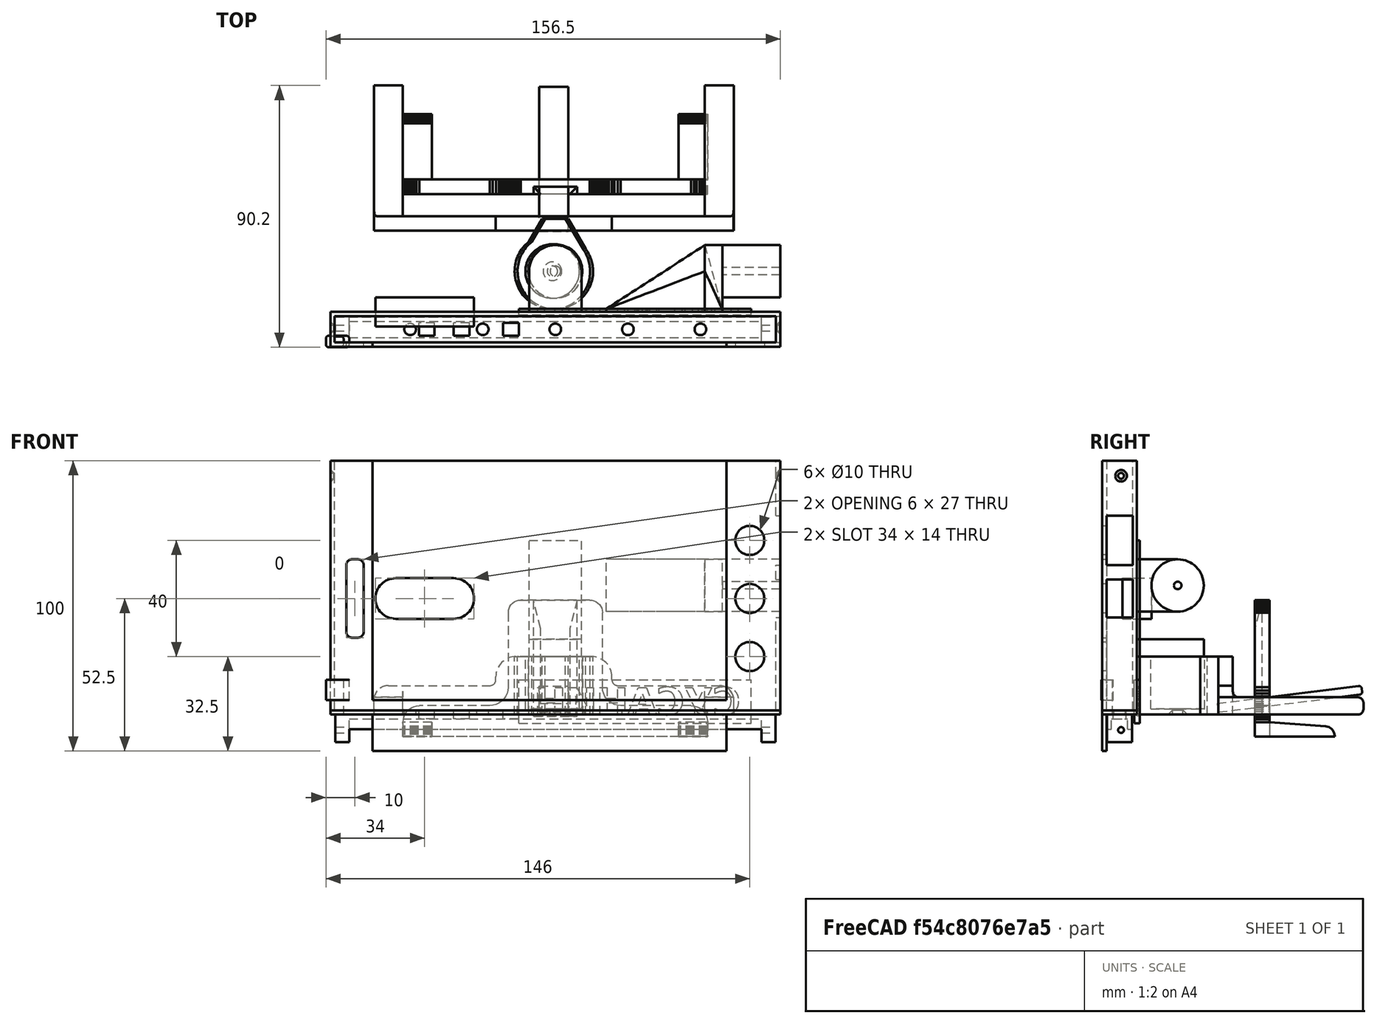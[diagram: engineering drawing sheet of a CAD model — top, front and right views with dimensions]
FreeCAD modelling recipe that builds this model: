
FCSTD DOCUMENT  (FreeCAD 0.18.4R)
Label: phone_nav_convertor
License: All rights reserved
LicenseURL: http://en.wikipedia.org/wiki/All_rights_reserved
objects: Part::Box×22, Part::Cylinder×9, Part::Fillet×8, Part::MultiFuse×7, Part::Feature×6, App::Part×6, Part::Cut×5, Part::FeaturePython×4, Part::Extrusion×4, Sketcher::SketchObject×3, Part::Compound×3, Mesh::Feature×2, Part::Part2DObjectPython×2, Part::RuledSurface×2, PartDesign::Body×2, Spreadsheet::Sheet×1, Part::Loft×1, PartDesign::Pad×1, PartDesign::FeatureBase×1, Part::Mirroring×1
note: 82 computed .brp shape members not serialized (recipe doc carries the construction recipe); baked Part::Feature solids carry a one-line shape summary decoded from their .brp

FEATURE [Part::Box] Box  label="pocket cube"
  AttacherType = Attacher::AttachEngine3D
  Height = 177
  Length = 152
  Placement = pos=(1.5,1.5,1.5) rot=(0,0,1;0rad)
  Width = 9
  expr: Placement.Base.x = p.wall
  expr: Placement.Base.y = p.wall
  expr: Placement.Base.z = p.wall
  expr: Height = p.phone_pocket_height + 100
  expr: Width = p.phone_pocket_width
  expr: Length = p.phone_pocket_length
FEATURE [Part::Box] Box001  label="wall cube"
  AttacherType = Attacher::AttachEngine3D
  Height = 87.5
  Length = 155
  Width = 12
  expr: Height = p.phone_pocket_height + 2 * p.wall + p.top_extra_height
  expr: Width = p.phone_pocket_width + 2 * p.wall
  expr: Length = p.phone_pocket_length + 2 * p.wall
FEATURE [Spreadsheet::Sheet] Spreadsheet  label="p"
  cells = A1=phone_pocket_width; B1(phone_pocket_width)=9; A2=phone_pocket_length; B2(phone_pocket_length)=152; A3=phone_pocket_height; B3(phone_pocket_height)=77; A4=wall; B4(wall)=1.5; A5=display_length; B5(display_length)=122; A6=display_height; B6(display_height)=70; A7=display_z_offset; B7(display_z_offset)==(p.phone_pocket_height - p.display_height) / 2; A8=display_btn_side_offset; B8(display_btn_side_offset)=16; A9=display_cam_side_offset; B9(display_cam_side_offset)=13; A10=cam_side_hole_length; B10(cam_side_hole_length)=6; A11=cam_side_hole_height; B11(cam_side_hole_height)=27; A12=cam_size_hole_z_offset; B12(cam_size_hole_z_offset)==(p.phone_pocket_height - p.cam_side_hole_height) / 2; A13=cam_side_hole_x_offset; B13(cam_side_hole_x_offset)=4; A14=speaker_height; B14(speaker_height)=17; A15=speaker_z_offset; B15(speaker_z_offset)=50; A16=usb_hole_height; B16(usb_hole_height)=13; A17=usb_hole_z_offset; B17(usb_hole_z_offset)=32; A18=top_extra_height; B18(top_extra_height)=7.5; A19=button_radius; B19(button_radius)=5; A20=button_z_dist; B20(button_z_dist)=20; A21=button_z_offset; B21(button_z_offset)==(p.phone_pocket_height - 2 * p.button_z_dist) / 2; A22=button_x_offset; B22(button_x_offset)=9; A23=cylinder_radius; B23(cylinder_radius)=9; A24=cylinder_height; B24(cylinder_height)=20; A25=cylinder_dist; B25(cylinder_dist)==p.phone_pocket_width + 2 * p.wall + p.cylinder_radius + 5; A26=enforcement_length; B26(enforcement_length)==p.cylinder_radius * 2; A27=enforcement_height; B27(enforcement_height)=40; A28=enforcement_width; B28(enforcement_width)=1; A29=bottom_hole_count; B29(bottom_hole_count)=5; A30=bottom_hole_dist; B30(bottom_hole_dist)=25; A31=bottom_hole_radius; B31(bottom_hole_radius)=2; A32=phone_btn1_offset; B32(phone_btn1_offset)=29; A33=phone_btn2_offset; B33(phone_btn2_offset)=41; A34=phone_btn3_offset; B34(phone_btn3_offset)=58; A35=phone_btn_length; B35(phone_btn_length)=5; A36=phone_btn_width; B36(phone_btn_width)=4; A37=camera_x_dist; B37(camera_x_dist)==p.phone_pocket_length - 21; A38=camera_y_dist; B38(camera_y_dist)==p.phone_pocket_height / 2; A39=camera_radius; B39(camera_radius)=7; A40=camera_finger_dist; B40(camera_finger_dist)=20; A41=finger_radius; B41(finger_radius)=7
FEATURE [Part::Box] Box002  label="display hole cube"
  AttacherType = Attacher::AttachEngine3D
  Height = 170
  Length = 122
  Placement = pos=(14.5,-10.5,5) rot=(0,0,1;0rad)
  Width = 20
  expr: Placement.Base.y = -p.phone_pocket_width - p.wall
  expr: Placement.Base.x = p.display_cam_side_offset + p.wall
  expr: Placement.Base.z = p.display_z_offset + p.wall
  expr: Height = p.display_height + 100
  expr: Length = p.display_length
FEATURE [Part::Box] Box003  label="speaker hole cube"
  AttacherType = Attacher::AttachEngine3D
  Height = 17
  Length = 10
  Placement = pos=(151,1.5,51.5) rot=(0,0,1;0rad)
  Width = 9
  expr: Placement.Base.y = p.wall
  expr: Width = p.phone_pocket_width
  expr: Placement.Base.z = p.speaker_z_offset + p.wall
  expr: Height = p.speaker_height
FEATURE [Part::Box] Box004  label="usb hole cube"
  AttacherType = Attacher::AttachEngine3D
  Height = 13
  Length = 10
  Placement = pos=(151,1.5,33.5) rot=(0,0,1;0rad)
  Width = 9
  expr: Placement.Base.y = p.wall
  expr: Placement.Base.z = p.usb_hole_z_offset + p.wall
  expr: Height = p.usb_hole_height
  expr: Width = p.phone_pocket_width
FEATURE [Part::Box] Box005  label="cam side hole cube"
  AttacherType = Attacher::AttachEngine3D
  Height = 27
  Length = 6
  Placement = pos=(5.5,-4,26.5) rot=(0,0,1;0rad)
  Width = 10
  expr: Placement.Base.x = p.wall + p.cam_side_hole_x_offset
  expr: Placement.Base.z = p.cam_size_hole_z_offset + p.wall
  expr: Height = p.cam_side_hole_height
  expr: Length = p.cam_side_hole_length
FEATURE [Part::Cylinder] Cylinder
  Angle = 360
  AttacherType = Attacher::AttachEngine3D
  Height = 10
  Placement = pos=(144.5,5,20) rot=(1,0,0;1.5708rad)
  Radius = 5
  expr: Placement.Base.x = p.wall + p.phone_pocket_length - p.button_x_offset
  expr: Placement.Base.z = p.button_z_offset + p.wall
FEATURE [Part::FeaturePython] Array  # Draft array (typed FeaturePython)
  Angle = 360
  ArrayType = 0
  Axis = (0,0,1)
  Base = -> Cylinder
  Center = (0,0,0)
  Fuse = false
  IntervalAxis = (0,0,0)
  IntervalX = (1,0,0)
  IntervalY = (0,1,0)
  IntervalZ = (0,0,20)
  NumberPolar = 1
  NumberX = 1
  NumberY = 1
  NumberZ = 3
  expr: IntervalZ.z = p.button_z_dist
FEATURE [Mesh::Feature] Plate
  Placement = pos=(68,34,26) rot=(-0.57735,-0.57735,0.57735;4.18879rad)
FEATURE [Part::Feature] Plate001
  Placement = pos=(0,31.2,0.6) rot=(0,0,1;0rad)
  shape: bbox 13 x 2.3 x 40 mm, 12 faces, 0 solids (baked)
FEATURE [Part::Cylinder] Cylinder001  label="side screw holes"
  Angle = 360
  AttacherType = Attacher::AttachEngine3D
  Height = 200
  Placement = pos=(-27,6.5,82.25) rot=(0,1,0;1.5708rad)
  Radius = 1
  expr: Placement.Base.z = p.wall + p.phone_pocket_height + p.top_extra_height / 2
FEATURE [Part::Cylinder] Cylinder002
  Angle = 360
  AttacherType = Attacher::AttachEngine3D
  Height = 20
  Placement = pos=(77.5,26,0) rot=(0,0,1;0rad)
  Radius = 9
  expr: Height = p.cylinder_height
  expr: Radius = p.cylinder_radius
  expr: Placement.Base.y = p.cylinder_dist
  expr: Placement.Base.x = p.phone_pocket_length / 2 + p.wall
FEATURE [Sketcher::SketchObject] Sketch
  MapMode = 5
  expr: Constraints[10] = p.cylinder_dist - 2 * p.wall - p.phone_pocket_width
  expr: Constraints[7] = p.cylinder_radius
  expr: Constraints[3] = p.cylinder_radius * 2
  expr: Constraints[9] = p.phone_pocket_length / 2 + p.wall - p.cylinder_radius
  expr: Constraints[8] = p.phone_pocket_width + 2 * p.wall
  sketch-geometry (4):
    g0: LineSegment StartX=68.5 StartY=12 StartZ=0 EndX=86.5 EndY=12 EndZ=0
    g1: LineSegment StartX=86.5 StartY=12 StartZ=0 EndX=86.5 EndY=26 EndZ=0
    g2: LineSegment StartX=68.5 StartY=12 StartZ=0 EndX=68.5 EndY=26 EndZ=0
    g3: ArcOfCircle CenterX=77.5 CenterY=26 CenterZ=0 NormalX=0 NormalY=0 NormalZ=1 AngleXU=0 Radius=9 StartAngle=0 EndAngle=3.14159
  constraints (11):
    c: Horizontal(g0)
    c: Coincident(g1,g0)
    c: Coincident(g2,g0)
    c: DistanceX(g0,g0) = 18
    c: DistanceY(g2,g1) = 0
    c: Tangent(g2,g3) = 1.5708
    c: Tangent(g3,g1) = -1.5708
    c: Radius(g3) = 9
    c: DistanceY(g-1,g0) = 12
    c: DistanceX(g-1,g0) = 68.5
    c: DistanceY(g2,g2) = 14
FEATURE [Part::Extrusion] Extrude
  Base = -> Sketch
  Dir = (0,0,1)
  DirMode = 2
  FaceMakerClass = Part::FaceMakerBullseye
  LengthFwd = 6
  LengthRev = 0
  Placement = pos=(0,0,20) rot=(0,0,1;0rad)
  Solid = true
  Symmetric = false
  expr: Placement.Base.z = p.cylinder_height
FEATURE [Part::Box] Box006  label="enforcement cube"
  AttacherType = Attacher::AttachEngine3D
  Height = 40
  Length = 18
  Placement = pos=(68.5,12,20) rot=(0,0,1;0rad)
  Width = 1
  expr: Placement.Base.y = p.phone_pocket_width + p.wall * 2
  expr: Placement.Base.x = p.phone_pocket_length / 2 + p.wall - p.enforcement_length / 2
  expr: Width = p.enforcement_width
  expr: Length = p.enforcement_length
  expr: Placement.Base.z = p.cylinder_height
  expr: Height = p.enforcement_height
FEATURE [Part::Cylinder] Cylinder003
  Angle = 360
  AttacherType = Attacher::AttachEngine3D
  Height = 100
  Placement = pos=(77.5,26,-50) rot=(0,0,1;0rad)
  Radius = 1.3
  expr: Placement.Base.y = p.cylinder_dist
  expr: Placement.Base.x = p.phone_pocket_length / 2 + p.wall
FEATURE [Part::Cut] Cut001  label="Cylinder Cut"
  Base = -> Cylinder002
  Tool = -> Cylinder003
FEATURE [Part::Cylinder] Cylinder004  label="bottom_hole"
  Angle = 360
  AttacherType = Attacher::AttachEngine3D
  Height = 20
  Placement = pos=(27.5,6,-10) rot=(0,0,1;0rad)
  Radius = 2
  expr: Radius = p.bottom_hole_radius
  expr: Placement.Base.x = (p.phone_pocket_length + 2 * p.wall - (p.bottom_hole_count - 1) * p.bottom_hole_dist) / 2
  expr: Placement.Base.y = p.wall + p.phone_pocket_width / 2
FEATURE [Part::FeaturePython] Array001  label="bottom hole array"  # Draft array (typed FeaturePython)
  Angle = 360
  ArrayType = 0
  Axis = (0,0,1)
  Base = -> Cylinder004
  Center = (0,0,0)
  Fuse = false
  IntervalAxis = (0,0,0)
  IntervalX = (25,0,0)
  IntervalY = (0,1,0)
  IntervalZ = (0,0,1)
  NumberPolar = 1
  NumberX = 5
  NumberY = 1
  NumberZ = 1
  expr: NumberX = p.bottom_hole_count
  expr: IntervalX.x = p.bottom_hole_dist
FEATURE [Part::Part2DObjectPython] ShapeString  # Draft 2D object (typed FeaturePython)
  FontFile = <path>
  Placement = pos=(141.21,12,0) rot=(0,0.707107,0.707107;3.14159rad)
  Size = 10
  String = СУСАНИН
  Tracking = 0
FEATURE [Part::Extrusion] Extrude001  label="Susanin_label"
  Base = -> ShapeString
  Dir = (1e-16,1,0)
  DirMode = 2
  FaceMakerClass = Part::FaceMakerBullseye
  LengthFwd = 10
  LengthRev = 0
  Solid = false
  Symmetric = false
FEATURE [Part::Box] Box007  label="Cube"
  AttacherType = Attacher::AttachEngine3D
  Height = 15
  Length = 80
  Placement = pos=(65,11,-3) rot=(0,0,1;0rad)
  Width = 2
FEATURE [Part::Cut] Cut002
  Base = -> Box007
  Tool = -> Extrude001
FEATURE [App::Part] Part001  label="label plate part"
  Group = -> [ShapeString,Extrude001,Box007,Cut002]
  Origin = -> Origin001
  Placement = pos=(-27,5,68) rot=(0,0,1;0rad)
FEATURE [Part::Part2DObjectPython] ShapeString001  # Draft 2D object (typed FeaturePython)
  FontFile = <path>
  Placement = pos=(141.21,12,0) rot=(0,0.707107,0.707107;3.14159rad)
  Size = 10
  String = СУСАНИН
  Tracking = 0
FEATURE [Part::Extrusion] Extrude002  label="Susanin_label001"
  Base = -> ShapeString001
  Dir = (0,1,-2e-16)
  DirMode = 2
  FaceMakerClass = Part::FaceMakerBullseye
  LengthFwd = 1
  LengthRev = 0
  Solid = false
  Symmetric = false
FEATURE [App::Part] Part002  label="label part"
  Group = -> [ShapeString001,Extrude002]
  Origin = -> Origin002
  Placement = pos=(-27,5,68) rot=(0,0,1;0rad)
FEATURE [Part::RuledSurface] Ruled_Surface
  Curve1 = -> Extrude [Edge10]
  Curve2 = -> Box006 [Edge12]
  Orientation = 0
FEATURE [Part::RuledSurface] Ruled_Surface001
  Curve1 = -> Box006 [Edge3]
  Curve2 = -> Box006 [Edge7]
  Orientation = 0
  Placement = pos=(68.5,12,20) rot=(0,0,1;0rad)
FEATURE [Part::Loft] Loft
  Closed = false
  MaxDegree = 5
  Ruled = true
  Sections = -> [Ruled_Surface,Ruled_Surface001]
  Solid = true
FEATURE [Part::MultiFuse] Fusion001
  Shapes = -> [Loft,Cut001]
FEATURE [Part::Feature] Box006_rev  label="enforcement cube (Rev)"
  Placement = pos=(68.5,12,20) rot=(0,0,1;0rad)
  shape: bbox 18 x 1 x 40 mm, 6 faces (baked)
FEATURE [Part::Feature] Extrude003  label="Extrude001"
  shape: bbox 18 x 23 x 6 mm, 6 faces (baked)
FEATURE [Part::Cylinder] Cylinder005  label="Cylinder004"
  Angle = 360
  AttacherType = Attacher::AttachEngine3D
  Height = 30
  Placement = pos=(77.5,26,2) rot=(0,0,1;0rad)
  Radius = 9.3
  expr: Radius = p.cylinder_radius + 0.3
FEATURE [Part::Cylinder] Cylinder006  label="Cylinder005"
  Angle = 360
  AttacherType = Attacher::AttachEngine3D
  Height = 20
  Placement = pos=(77.5,26,0) rot=(0,0,1;0rad)
  Radius = 13
  expr: Height = p.cylinder_height
  expr: Radius = p.cylinder_radius + 4
FEATURE [PartDesign::Body] Body
  Origin = -> Origin004
  Placement = pos=(-0.4,0.5,0) rot=(0,0,1;0rad)
FEATURE [Sketcher::SketchObject] Sketch001
  MapMode = 5
  sketch-geometry (4):
    g0: LineSegment StartX=74 StartY=44 StartZ=0 EndX=68 EndY=33.7847 EndZ=0
    g1: LineSegment StartX=68 StartY=33.7847 StartZ=0 EndX=88 EndY=33.7847 EndZ=0
    g2: LineSegment StartX=88 StartY=33.7847 StartZ=0 EndX=82 EndY=44 EndZ=0
    g3: LineSegment StartX=82 StartY=44 StartZ=0 EndX=74 EndY=44 EndZ=0
  constraints (10):
    c: Coincident(g0,g1)
    c: Horizontal(g1)
    c: Coincident(g1,g2)
    c: Coincident(g2,g3)
    c: Coincident(g3,g0)
    c: Horizontal(g3)
    c: DistanceX(g3,g3) = 8
    c: DistanceX(g-1,g0) = 74
    c: DistanceX(g2,g1) = 6
    c: DistanceX(g0,g0) = 6
FEATURE [PartDesign::Pad] Pad
  Length = 20
  Length2 = 100
  Profile = -> Sketch001
  Type = 0
FEATURE [Part::MultiFuse] Fusion002
  Shapes = -> [Cylinder006,Pad]
FEATURE [Part::Cylinder] Cylinder007  label="Cylinder006"
  Angle = 360
  AttacherType = Attacher::AttachEngine3D
  Height = 30
  Placement = pos=(77.5,26,0) rot=(0,0,1;0rad)
  Radius = 1.8
FEATURE [Part::MultiFuse] Fusion003
  Shapes = -> [Cylinder005,Cylinder007]
FEATURE [Part::Cut] Cut003
  Base = -> Fusion002
  Tool = -> Fusion003
FEATURE [Part::FeaturePython] Countersunk001  # WARN: FeaturePython — macro-defined, semantics opaque (R4)
  Placement = pos=(-1,0,0) rot=(0,0,1;0rad)
  baseObject = -> Cut003
  diameters = Edge10:M3:0:0:Default
FEATURE [Part::Box] Box008  label="Cube001"
  AttacherType = Attacher::AttachEngine3D
  Height = 1.5
  Length = 155
  Width = 12
  expr: Height = p.wall
  expr: Width = p.phone_pocket_width + 2 * p.wall
  expr: Length = p.phone_pocket_length + 2 * p.wall
FEATURE [Part::Box] Box009  label="Cube002"
  AttacherType = Attacher::AttachEngine3D
  Height = 9.5
  Length = 151.6
  Placement = pos=(1.7,1.7,-9.5) rot=(0,0,1;0rad)
  Width = 8.6
  expr: Width = p.phone_pocket_width - 0.4
  expr: Length = p.phone_pocket_length - 0.4
  expr: Height = p.wall + p.top_extra_height + 0.5
  expr: Placement.Base.z = -p.top_extra_height - p.wall - 0.5
  expr: Placement.Base.y = p.wall + 0.2
  expr: Placement.Base.x = p.wall + 0.2
FEATURE [Part::Box] Box010  label="Cube003"
  AttacherType = Attacher::AttachEngine3D
  Height = 9.5
  Length = 142
  Placement = pos=(6.5,3.2,-11) rot=(0,0,1;0rad)
  Width = 5.6
  expr: Width = p.phone_pocket_width - 2 * p.wall - 0.4
  expr: Length = p.phone_pocket_length - 10
  expr: Height = p.top_extra_height + 2
  expr: Placement.Base.z = -p.wall - p.top_extra_height - 2
  expr: Placement.Base.y = p.wall * 2 + 0.2
  expr: Placement.Base.x = p.wall + 5
FEATURE [Part::Cylinder] Cylinder008  label="side screw holes001"
  Angle = 360
  AttacherType = Attacher::AttachEngine3D
  Height = 200
  Placement = pos=(-27,6.5,-5.3) rot=(0,1,0;1.5708rad)
  Radius = 1
FEATURE [Mesh::Feature] Support2_0  label="Support2.0"
FEATURE [Part::Feature] Support2_0001  label="Support2 shape"
  Placement = pos=(130,69,-24) rot=(0,0,1;3.14159rad)
  shape: bbox 105 x 27.5 x 47.09 mm, 356 faces, 0 solids (baked)
FEATURE [Part::Feature] Support2_0001_solid  label="Support2 shape (Solid)"
  shape: bbox 105 x 27.5 x 47.09 mm, 356 faces (baked)
FEATURE [Part::Box] Box013  label="btn cube"
  AttacherType = Attacher::AttachEngine3D
  Height = 12
  Length = 4.6
  Width = 3.6
  expr: Height = p.top_extra_height + 3 + p.wall
  expr: Width = p.phone_btn_width - 0.4
  expr: Length = p.phone_btn_length - 0.4
FEATURE [Part::Box] Box014  label="btn hole cube1"
  AttacherType = Attacher::AttachEngine3D
  Height = 20
  Length = 5.4
  Placement = pos=(30.5,3.8,-7.5) rot=(0,0,1;0rad)
  Width = 4.4
  expr: Placement.Base.x = p.wall + p.phone_btn1_offset
  expr: Placement.Base.y = p.wall + p.phone_pocket_width / 2 - p.phone_btn_width / 2 - 0.2
  expr: Placement.Base.z = -p.top_extra_height
  expr: Width = p.phone_btn_width + 0.4
  expr: Length = p.phone_btn_length + 0.4
FEATURE [Part::Box] Box015  label="btn hole cube2"
  AttacherType = Attacher::AttachEngine3D
  Height = 20
  Length = 5.4
  Placement = pos=(42.5,3.8,-7.5) rot=(0,0,1;0rad)
  Width = 4.4
  expr: Placement.Base.x = p.wall + p.phone_btn2_offset
  expr: Placement.Base.y = p.wall + p.phone_pocket_width / 2 - p.phone_btn_width / 2 - 0.2
  expr: Placement.Base.z = -p.top_extra_height
  expr: Width = p.phone_btn_width + 0.4
  expr: Length = p.phone_btn_length + 0.4
FEATURE [Part::Box] Box016  label="btn hole cube3"
  AttacherType = Attacher::AttachEngine3D
  Height = 20
  Length = 5.4
  Placement = pos=(59.5,3.8,-7.5) rot=(0,0,1;0rad)
  Width = 4.4
  expr: Placement.Base.x = p.wall + p.phone_btn3_offset
  expr: Placement.Base.y = p.wall + p.phone_pocket_width / 2 - p.phone_btn_width / 2 - 0.2
  expr: Placement.Base.z = -p.top_extra_height
  expr: Width = p.phone_btn_width + 0.4
  expr: Length = p.phone_btn_length + 0.4
FEATURE [Part::Box] Box017  label="btn rim cube"
  AttacherType = Attacher::AttachEngine3D
  Height = 7
  Length = 8
  Placement = pos=(-1.5,-0.2,5) rot=(0,0,1;0rad)
  Width = 4
  expr: Placement.Base.x = -p.wall
  expr: Height = p.top_extra_height + 3 + p.wall - 5
  expr: Width = p.phone_btn_width
  expr: Length = p.phone_btn_length + 2 * p.wall
FEATURE [Part::Box] Box018  label="Cube006"
  AttacherType = Attacher::AttachEngine3D
  Height = 12.5
  Length = 121.8
  Placement = pos=(14.6,0,-12.5) rot=(0,0,1;0rad)
  Width = 1.5
  expr: Width = p.wall
  expr: Length = p.display_length - 0.2
  expr: Height = (p.phone_pocket_height - p.display_height) / 2 + p.top_extra_height + p.wall
  expr: Placement.Base.z = -(p.phone_pocket_height - p.display_height) / 2 - p.top_extra_height - p.wall
  expr: Placement.Base.x = p.display_cam_side_offset + p.wall + 0.1
FEATURE [Part::MultiFuse] Fusion004
  Shapes = -> [Box008,Box009,Box018]
FEATURE [Part::Box] Box019  label="Cube007"
  AttacherType = Attacher::AttachEngine3D
  Height = 6
  Length = 142
  Placement = pos=(6.5,1.5,-11) rot=(0,0,1;0rad)
  Width = 9
  expr: Width = p.phone_pocket_width
  expr: Length = p.phone_pocket_length - 10
  expr: Height = 6
  expr: Placement.Base.z = -p.wall - p.top_extra_height - 2
  expr: Placement.Base.y = p.wall
  expr: Placement.Base.x = p.wall + 5
FEATURE [Part::MultiFuse] Fusion005
  Shapes = -> [Box010,Cylinder008,Box014,Box015,Box016,Box019]
FEATURE [Part::Cut] Cut004
  Base = -> Fusion004
  Tool = -> Fusion005
FEATURE [App::Part] Part004  label="lid part"
  Group = -> [Box008,Box009,Box010,Fusion004,Cut004,Cylinder008,Fusion005,Box014,Box015,Box016,Box018,Box019]
  Origin = -> Origin005
  Placement = pos=(0,0,87.5) rot=(0,0,1;0rad)
  expr: Placement.Base.z = p.wall * 2 + p.phone_pocket_height + p.top_extra_height
FEATURE [Part::Fillet] Fillet001
  Base = -> Box005
  Edges = 4 edges r=2: [Edge2,Edge4,Edge6,Edge8]
FEATURE [Part::Fillet] Fillet002
  Base = -> Box013
  Edges = 4 edges r=1: [Edge1,Edge3,Edge5,Edge7]
FEATURE [Part::Compound] Compound  label="adapter2adapter compaund"
  Links = -> [Fusion001,Box006_rev,Extrude003]
FEATURE [PartDesign::FeatureBase] Clone
  BaseFeature = -> Compound
FEATURE [PartDesign::Body] Body001  label="adapter2adapter clone"
  BaseFeature = -> Compound
  Group = -> [Clone]
  Origin = -> Origin007
  Placement = pos=(155,0,-33) rot=(0,-1,0;1.5708rad)
  Tip = -> Clone
FEATURE [Part::Feature] Extrude005001  label="camera finger hole001"
  shape: bbox 34 x 10 x 14 mm, 6 faces (baked)
FEATURE [Part::MultiFuse] Fusion
  Shapes = -> [Box,Box002,Box003,Box004,Array,Cylinder001,Array001,Fillet001,Extrude005001]
FEATURE [Part::Cut] Cut
  Base = -> Box001
  Tool = -> Fusion
FEATURE [Sketcher::SketchObject] Sketch002  label="camera finger hole sketch"
  MapMode = 5
  Placement = pos=(0,12,0) rot=(0,0.707107,0.707107;3.14159rad)
  Support = -> [Cut]
  expr: Constraints[8] = p.phone_pocket_length - p.camera_x_dist + p.wall
  expr: Constraints[7] = p.camera_y_dist + p.wall
  expr: Constraints[6] = p.camera_finger_dist
  expr: Constraints[5] = p.finger_radius
  sketch-geometry (4):
    g0: ArcOfCircle CenterX=-22.5 CenterY=40 CenterZ=0 NormalX=0 NormalY=0 NormalZ=1 AngleXU=0 Radius=7 StartAngle=4.71239 EndAngle=7.85398
    g1: ArcOfCircle CenterX=-42.5 CenterY=40 CenterZ=0 NormalX=0 NormalY=0 NormalZ=1 AngleXU=0 Radius=7 StartAngle=1.5708 EndAngle=4.71239
    g2: LineSegment StartX=-22.5 StartY=47 StartZ=0 EndX=-42.5 EndY=47 EndZ=0
    g3: LineSegment StartX=-22.5 StartY=33 StartZ=0 EndX=-42.5 EndY=33 EndZ=0
  constraints (10):
    c: Tangent(g0,g3) = 1.5708
    c: Tangent(g0,g2) = -1.5708
    c: Tangent(g2,g1) = -1.5708
    c: Tangent(g3,g1) = 1.5708
    c: Equal(g0,g1)
    c: Radius(g0) = 7
    c: DistanceX(g1,g0) = 20
    c: DistanceY(g-1,g0) = 40
    c: DistanceX(g0,g-1) = 22.5
    c: Horizontal(g2)
FEATURE [Part::Extrusion] Extrude005  label="camera finger hole"
  Base = -> Sketch002
  Dir = (0,1,-2e-16)
  DirMode = 2
  FaceMakerClass = Part::FaceMakerBullseye
  LengthFwd = 10
  LengthRev = 0
  Solid = true
  Symmetric = true
FEATURE [Part::FeaturePython] Countersunk  # WARN: FeaturePython — macro-defined, semantics opaque (R4)
  baseObject = -> Cut
  diameters = Edge5:M2:0:0:Default | Edge47:M2:0:0:Default
FEATURE [App::Part] Part  label="telephone frame part"
  Group = -> [Box,Box001,Cut,Box002,Fusion,Box003,Box004,Box005,Cylinder,Array,Cylinder001,Cylinder002,Sketch,Extrude,Box006,Cylinder003,Cut001,Cylinder004,Array001,Ruled_Surface,Ruled_Surface001,Loft,Fusion001,Box006_rev,Extrude003,Plate,Fillet001,Compound,Body001,Sketch002,Extrude005,Extrude005001,Countersunk]
  Origin = -> Origin
FEATURE [Part::Box] Box022  label="Cube008"
  AttacherType = Attacher::AttachEngine3D
  Height = 6
  Length = 10
  Placement = pos=(15,40,0) rot=(0,0,1;0rad)
  Width = 50
FEATURE [Part::Box] Box023  label="Cube009"
  AttacherType = Attacher::AttachEngine3D
  Height = 10
  Length = 124
  Placement = pos=(15,40,0) rot=(0,0,1;0rad)
  Width = 5
FEATURE [Part::Box] Box024  label="Cube010"
  AttacherType = Attacher::AttachEngine3D
  Height = 10
  Length = 40
  Placement = pos=(57,40,10) rot=(0,0,1;0rad)
  Width = 5
FEATURE [Part::Fillet] Fillet
  Base = -> Box024
  Edges = 2 edges r=7: [Edge2,Edge6]
FEATURE [Part::Fillet] Fillet003
  Base = -> Box023
  Edges = 2 edges r=5: [Edge2,Edge6]
FEATURE [Part::Fillet] Fillet004
  Base = -> Box022
  Edges = 2 edges r=2: [Edge11,Edge12]
FEATURE [Part::Mirroring] Part__Mirroring  label="Cube008 (Mirror #1)"
  Base = (77,0,0)
  Normal = (1,0,0)
  Source = -> Fillet004
FEATURE [Part::MultiFuse] Fusion006
  Shapes = -> [Part__Mirroring,Fillet004,Fillet,Fillet003]
FEATURE [Part::Fillet] Fillet005
  Base = -> Fusion006
  Edges = 4 edges r=2: [Edge23,Edge35,Edge48,Edge54]
FEATURE [Part::Box] Box025  label="Cube011"
  AttacherType = Attacher::AttachEngine3D
  Height = 3
  Length = 10
  Placement = pos=(18,40,0) rot=(0,0,1;0rad)
  Width = 50
FEATURE [Part::Fillet] Fillet006
  Base = -> Box025
  Edges = 2 edges r=1: [Edge11,Edge12]
  Placement = pos=(54,0.348623,-3.98478) rot=(1,0,0;0.122173rad)
FEATURE [Part::Compound] Compound001
  Links = -> [Countersunk001,Fillet005,Fillet006]
FEATURE [App::Part] Part003  label="adapter part"
  Group = -> [Plate001,Cut003,Fusion002,Cylinder005,Cylinder006,Body,Cylinder007,Pad,Sketch001,Fusion003,Countersunk001,Support2_0,Support2_0001,Support2_0001_solid,Compound001,Box022,Box023,Part__Mirroring,Box024,Fillet,Fillet003,Fillet004,Fusion006,Fillet005,Fillet006]
  Origin = -> Origin003
FEATURE [Part::Fillet] Fillet007
  Base = -> Box017
  Edges = 4 edges r=1: [Edge1,Edge3,Edge5,Edge7]
FEATURE [Part::Compound] Compound002  label="button compound"
  Links = -> [Fillet002,Fillet007]
FEATURE [App::Part] Part005  label="button part"
  Group = -> [Box013,Box017,Fillet002,Fillet007,Compound002]
  Origin = -> Origin006
  Placement = pos=(30.8,4.1,77.4) rot=(0,0,1;0rad)
note: 2 file-system paths scrubbed to <path> (originals preserved in the JSON sidecar)
